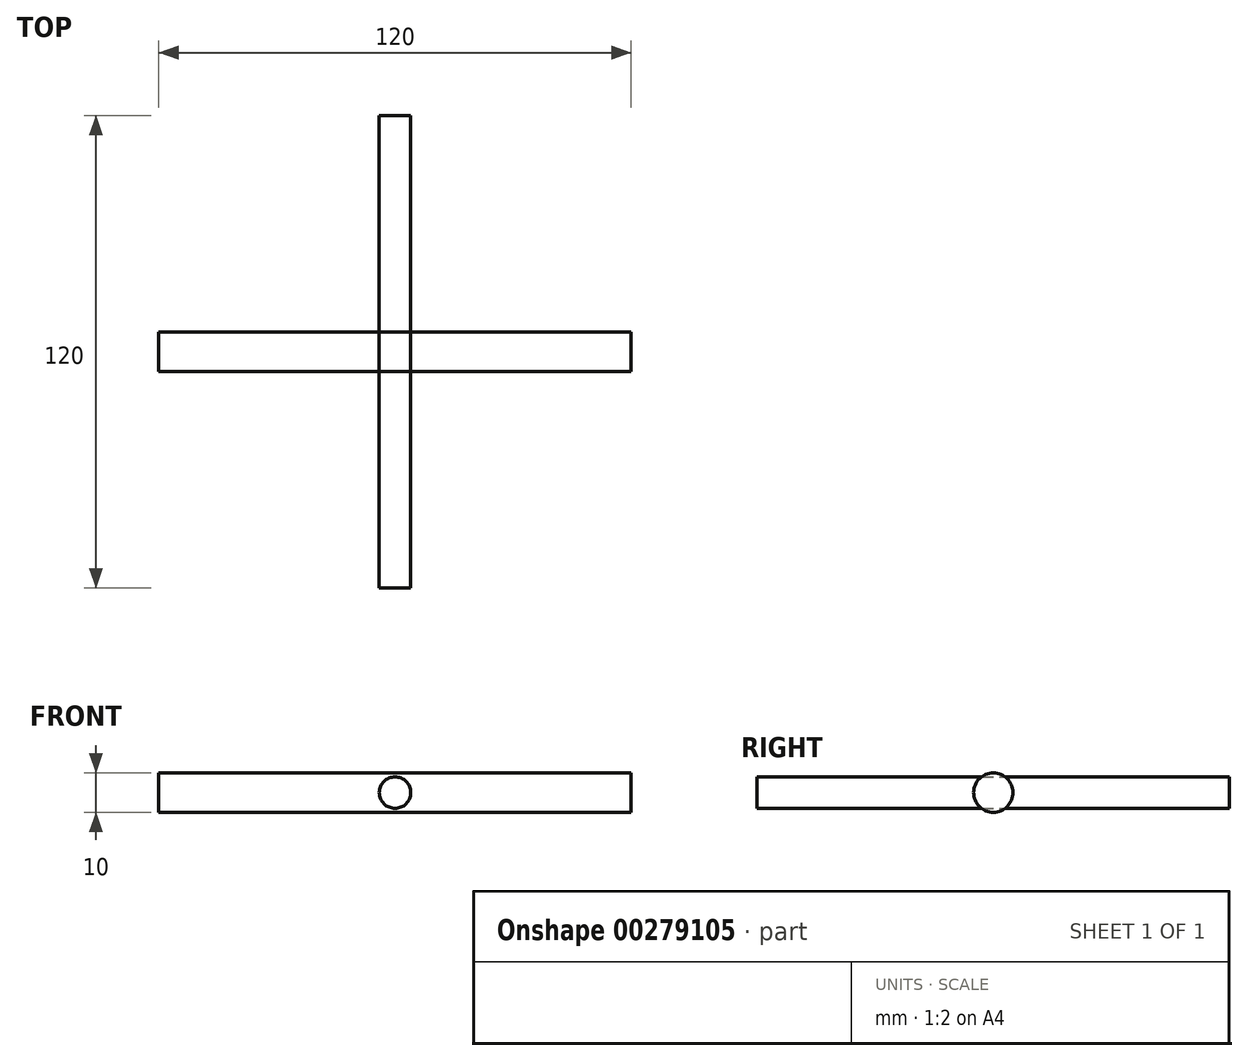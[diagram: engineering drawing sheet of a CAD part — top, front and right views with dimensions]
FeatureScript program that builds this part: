
annotation { "Feature Type Name" : "Feature", "Feature Type Description" : "" }
export const myFeature = defineFeature(function(context is Context, id is Id, definition is map)
    precondition{}
    {
        {
            var Q0;
            Q0=qCreatedBy(makeId("Front.planeOp"),FACE);
            var sketch = newSketch(context, id + "F0", { "sketchPlane" : qUnion([Q0])});
            skCircle(sketch, "E0", {"center": v(0, 0) * mm, "radius": 4 * mm});
            skSolve(sketch);
        }
        {
            var Q0;
            Q0=makeQuery(id+"F0.imprint","IMPRINT",FACE,{"disambiguationData":[TD([[makeQuery(id+"F0.imprint","IMPRINT",EDGE,{"derivedFrom":sQuery(id+"F0.wireOp",EDGE,"E0")}),1.0]])]});
            extrude(context, id + "F1", {"entities" : qUnion([Q0]), "depth" : 120 * mm});
        }
        {
            var Q0;
            Q0=qCreatedBy(makeId("Right.planeOp"),FACE);
            var sketch = newSketch(context, id + "F2", { "sketchPlane" : qUnion([Q0])});
            skLineSegment(sketch, "E1", {"start": v(0, 0) * mm, "end": v(-60, 0) * mm});
            skCircle(sketch, "E2", {"center": v(-60, 0) * mm, "radius": 5 * mm});
            skSolve(sketch);
        }
        {
            var Q0;
            Q0=makeQuery(id+"F2.imprint","IMPRINT",FACE,{"disambiguationData":[TD([[makeQuery(id+"F2.imprint","IMPRINT",EDGE,{"derivedFrom":sQuery(id+"F2.wireOp",EDGE,"E2")}),1.0]])]});
            var Q1;
            Q1=sQuery(id+"F2.wireOp",EDGE,"E2");
            extrude(context, id + "F3", {"entities" : qUnion([Q0]), "surfaceEntities" : qUnion([Q1]), "depth" : 60 * mm, "hasSecondDirection" : true, "secondDirectionOppositeDirection" : true, "secondDirectionDepth" : 60 * mm});
        }
    });
